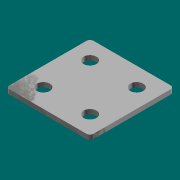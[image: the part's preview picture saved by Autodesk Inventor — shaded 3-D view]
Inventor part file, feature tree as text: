
AUTODESK INVENTOR PART (.ipt)
format: ipt  version: 2016 (Build 200138000, 138)  size: 123,392 bytes
history: native  units: mm
features: other x63, extrude x1, sketch x1
ambient origin geometry x8: Origin, YZ Plane, XZ Plane, XY Plane, X Axis, Y Axis, Z Axis, Center Point
bodies: Solid1 (feature_tree)
feature tree (65):
  extrude  "Extrusion1"  [1 undecoded]
  other  "to_bolt1_XY"
  other  "to_bolt1_YZ"
  other  "to_bolt1_ZX"
  other  "to_bolt1_X"
  other  "to_bolt1_Y"
  other  "to_bolt1_Z"
  other  "to_bolt1_Center"
  other  "to_bolt2_XY"
  other  "to_bolt2_YZ"
  other  "to_bolt2_ZX"
  other  "to_bolt2_X"
  other  "to_bolt2_Y"
  other  "to_bolt2_Z"
  other  "to_bolt2_Center"
  other  "to_dummy_XY"
  other  "to_dummy_YZ"
  other  "to_dummy_ZX"
  other  "to_dummy_X"
  other  "to_dummy_Y"
  other  "to_dummy_Z"
  other  "to_dummy_Center"
  other  "to_nut1_XY"
  other  "to_nut1_YZ"
  other  "to_nut1_ZX"
  other  "to_nut1_X"
  other  "to_nut1_Y"
  other  "to_nut1_Z"
  other  "to_nut1_Center"
  other  "to_nut2_XY"
  other  "to_nut2_YZ"
  other  "to_nut2_ZX"
  other  "to_nut2_X"
  other  "to_nut2_Y"
  other  "to_nut2_Z"
  other  "to_nut2_Center"
  other  "x1_to_bolt_XY"
  other  "x1_to_bolt_YZ"
  other  "x1_to_bolt_ZX"
  other  "x1_to_bolt_X"
  other  "x1_to_bolt_Y"
  other  "x1_to_bolt_Z"
  other  "x1_to_bolt_Center"
  other  "x2_to_bolt_XY"
  other  "x2_to_bolt_YZ"
  other  "x2_to_bolt_ZX"
  other  "x2_to_bolt_X"
  other  "x2_to_bolt_Y"
  other  "x2_to_bolt_Z"
  other  "x2_to_bolt_Center"
  other  "x3_to_bolt_XY"
  other  "x3_to_bolt_YZ"
  other  "x3_to_bolt_ZX"
  other  "x3_to_bolt_X"
  other  "x3_to_bolt_Y"
  other  "x3_to_bolt_Z"
  other  "x3_to_bolt_Center"
  other  "x4_to_bolt_XY"
  other  "x4_to_bolt_YZ"
  other  "x4_to_bolt_ZX"
  other  "x4_to_bolt_X"
  other  "x4_to_bolt_Y"
  other  "x4_to_bolt_Z"
  other  "x4_to_bolt_Center"
  sketch  "Sketch_1"  dims[d0=2.0mm d1=0.0mm d2=0.0mm d3=0.0mm d4=0.0mm d5=0.0mm d6=0.0mm d7=0.0mm]
note: 1 required parameter value undecoded (feature->parameter linkage not recoverable at this tier; creation-order binding heuristic only, values carry confidence <= 0.55)
